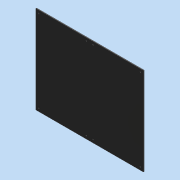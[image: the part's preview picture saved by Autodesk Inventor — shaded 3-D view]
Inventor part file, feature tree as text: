
AUTODESK INVENTOR PART (.ipt)
format: ipt  version: 2016 (Build 200138000, 138)  size: 105,472 bytes
history: native  units: mm
features: hole x8, extrude x1, sketch x1
ambient origin geometry x8: Origin, YZ Plane, XZ Plane, XY Plane, X Axis, Y Axis, Z Axis, Center Point
bodies: Solid1 (feature_tree)
feature tree (10):
  extrude  "Extrusion1"  Depth=360.0mm
  hole  "Hole1"  [1 undecoded]
  hole  "Hole2"  [1 undecoded]
  hole  "Hole3"  [1 undecoded]
  hole  "Hole4"  [1 undecoded]
  hole  "Hole5"  [1 undecoded]
  hole  "Hole6"  [1 undecoded]
  hole  "Hole7"  [1 undecoded]
  hole  "Hole8"  [1 undecoded]
  sketch  "Sketch1"  dims[d0=440.0mm d1=360.0mm d2=3.0mm d3=0.0mm d4=12.0mm d5=12.0mm d6=4.0mm d7=6.0mm d8=4.0mm d9=2.0mm d10=90.0deg d11=8.0mm d12=20.594885mm d13=12.0mm d14=12.0mm d15=4.0mm d16=6.0mm d17=4.0mm d18=2.0mm d19=90.0deg d20=8.0mm d21=20.594885mm d22=12.0mm d23=12.0mm d24=4.0mm d25=6.0mm d26=4.0mm d27=2.0mm d28=90.0deg d29=8.0mm d30=20.594885mm d31=12.0mm d32=12.0mm d33=4.0mm d34=6.0mm d35=4.0mm d36=2.0mm d37=90.0deg d38=8.0mm d39=20.594885mm d40=12.0mm d41=206.5mm d42=4.0mm d43=6.0mm d44=4.0mm d45=2.0mm d46=90.0deg d47=8.0mm d48=20.594885mm d49=12.0mm d50=206.5mm d51=4.0mm d52=6.0mm d53=4.0mm d54=2.0mm d55=90.0deg d56=8.0mm d57=20.594885mm d58=12.0mm d59=206.5mm d60=4.0mm d61=6.0mm d62=4.0mm d63=2.0mm d64=90.0deg d65=8.0mm d66=20.594885mm d67=12.0mm d68=206.5mm d69=4.0mm d70=6.0mm d71=4.0mm d72=2.0mm d73=90.0deg d74=8.0mm d75=20.594885mm]
note: 8 required parameter values undecoded (feature->parameter linkage not recoverable at this tier; creation-order binding heuristic only, values carry confidence <= 0.55)
